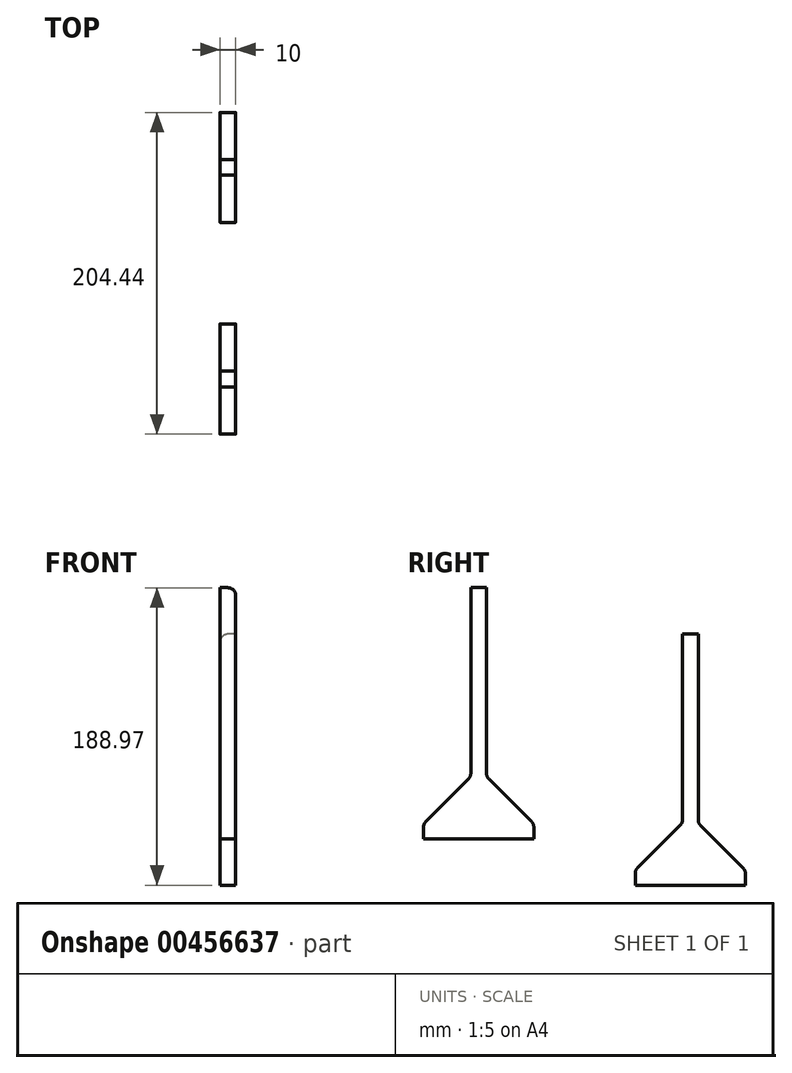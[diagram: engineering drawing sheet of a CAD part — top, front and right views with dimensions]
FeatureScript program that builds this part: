
annotation { "Feature Type Name" : "Feature", "Feature Type Description" : "" }
export const myFeature = defineFeature(function(context is Context, id is Id, definition is map)
    precondition{}
    {
        {
            var Q0;
            Q0=qCreatedBy(makeId("Right.planeOp"),FACE);
            var sketch = newSketch(context, id + "F0", { "sketchPlane" : qUnion([Q0])});
            skLineSegment(sketch, "E0", {"start": v(-4.56, 141.63) * mm, "end": v(-4.56, -8.37) * mm});
            skLineSegment(sketch, "E1", {"start": v(-4.56, 141.63) * mm, "end": v(5.44, 141.63) * mm});
            skLineSegment(sketch, "E2", {"start": v(5.44, 141.63) * mm, "end": v(5.44, -8.37) * mm});
            skLineSegment(sketch, "E3", {"start": v(-4.56, -8.37) * mm, "end": v(5.44, -8.37) * mm});
            skLineSegment(sketch, "E4", {"start": v(-4.56, -8.37) * mm, "end": v(-34.56, -8.37) * mm});
            skLineSegment(sketch, "E5", {"start": v(-34.56, -8.37) * mm, "end": v(-34.56, -17.85) * mm});
            skLineSegment(sketch, "E6", {"start": v(-34.56, -17.85) * mm, "end": v(35.44, -17.85) * mm});
            skLineSegment(sketch, "E7", {"start": v(5.44, -8.37) * mm, "end": v(35.44, -8.37) * mm});
            skLineSegment(sketch, "E8", {"start": v(35.44, -8.37) * mm, "end": v(35.44, -17.85) * mm});
            skLineSegment(sketch, "E9", {"start": v(-34.56, -8.37) * mm, "end": v(-4.56, 21.63) * mm});
            skLineSegment(sketch, "E10", {"start": v(-4.56, 21.63) * mm, "end": v(-4.56, -8.37) * mm});
            skLineSegment(sketch, "E11", {"start": v(5.44, -8.37) * mm, "end": v(5.44, 21.63) * mm});
            skLineSegment(sketch, "E12", {"start": v(5.44, 21.63) * mm, "end": v(35.44, -8.37) * mm});
            skLineSegment(sketch, "E13", {"start": v(129.88, 112.15) * mm, "end": v(129.88, -37.85) * mm});
            skLineSegment(sketch, "E14", {"start": v(129.88, 112.15) * mm, "end": v(139.88, 112.15) * mm});
            skLineSegment(sketch, "E15", {"start": v(139.88, 112.15) * mm, "end": v(139.88, -37.85) * mm});
            skLineSegment(sketch, "E16", {"start": v(129.88, -37.85) * mm, "end": v(139.88, -37.85) * mm});
            skLineSegment(sketch, "E17", {"start": v(129.88, -37.85) * mm, "end": v(99.88, -37.85) * mm});
            skLineSegment(sketch, "E18", {"start": v(99.88, -37.85) * mm, "end": v(99.88, -47.34) * mm});
            skLineSegment(sketch, "E19", {"start": v(99.88, -47.34) * mm, "end": v(169.88, -47.34) * mm});
            skLineSegment(sketch, "E20", {"start": v(139.88, -37.85) * mm, "end": v(169.88, -37.85) * mm});
            skLineSegment(sketch, "E21", {"start": v(169.88, -37.85) * mm, "end": v(169.88, -47.34) * mm});
            skLineSegment(sketch, "E22", {"start": v(99.88, -37.85) * mm, "end": v(129.88, -7.85) * mm});
            skLineSegment(sketch, "E23", {"start": v(129.88, -7.85) * mm, "end": v(129.88, -37.85) * mm});
            skLineSegment(sketch, "E24", {"start": v(139.88, -37.85) * mm, "end": v(139.88, -7.85) * mm});
            skLineSegment(sketch, "E25", {"start": v(139.88, -7.85) * mm, "end": v(169.88, -37.85) * mm});
            skSolve(sketch);
        }
        {
            var Q0;
            Q0=makeQuery(id+"F0.imprint","IMPRINT",FACE,{"disambiguationData":[TD([[makeQuery(id+"F0.imprint","IMPRINT",EDGE,{"derivedFrom":sQuery(id+"F0.wireOp",EDGE,"E0")}),1.0]])]});
            var Q1;
            Q1=makeQuery(id+"F0.imprint","IMPRINT",FACE,{"disambiguationData":[TD([[makeQuery(id+"F0.imprint","IMPRINT",EDGE,{"derivedFrom":sQuery(id+"F0.wireOp",EDGE,"E4")}),-1.0]])]});
            var Q2;
            Q2=makeQuery(id+"F0.imprint","IMPRINT",FACE,{"disambiguationData":[TD([[makeQuery(id+"F0.imprint","IMPRINT",EDGE,{"derivedFrom":sQuery(id+"F0.wireOp",EDGE,"E7")}),1.0]])]});
            var Q3;
            Q3=makeQuery(id+"F0.imprint","IMPRINT",FACE,{"disambiguationData":[TD([[makeQuery(id+"F0.imprint","IMPRINT",EDGE,{"derivedFrom":sQuery(id+"F0.wireOp",EDGE,"E3")}),-1.0]])]});
            extrude(context, id + "F1", {"entities" : qUnion([Q0, Q1, Q2, Q3]), "depth" : 10 * mm});
        }
        {
            var Q0;
            Q0=makeQuery(id+"F0.imprint","IMPRINT",FACE,{"disambiguationData":[TD([[makeQuery(id+"F0.imprint","IMPRINT",EDGE,{"derivedFrom":sQuery(id+"F0.wireOp",EDGE,"E13")}),1.0]])]});
            var Q1;
            Q1=makeQuery(id+"F0.imprint","IMPRINT",FACE,{"disambiguationData":[TD([[makeQuery(id+"F0.imprint","IMPRINT",EDGE,{"derivedFrom":sQuery(id+"F0.wireOp",EDGE,"E17")}),-1.0]])]});
            var Q2;
            Q2=makeQuery(id+"F0.imprint","IMPRINT",FACE,{"disambiguationData":[TD([[makeQuery(id+"F0.imprint","IMPRINT",EDGE,{"derivedFrom":sQuery(id+"F0.wireOp",EDGE,"E20")}),1.0]])]});
            var Q3;
            Q3=makeQuery(id+"F0.imprint","IMPRINT",FACE,{"disambiguationData":[TD([[makeQuery(id+"F0.imprint","IMPRINT",EDGE,{"derivedFrom":sQuery(id+"F0.wireOp",EDGE,"E16")}),-1.0]])]});
            extrude(context, id + "F2", {"entities" : qUnion([Q0, Q1, Q2, Q3]), "depth" : 10 * mm});
        }
        {
            var Q0;
            Q0=makeQuery(id+"F1.opExtrude","CAP_EDGE",EDGE,{"disambiguationData":[OSD([sQuery(id+"F0.wireOp",EDGE,"E1")])],"isStart":false});
            fillet(context, id + "F3", {"entities" : qUnion([Q0]), "radius" : 5.08 * mm, "tangentPropagation" : true, "allowEdgeOverflow" : false});
        }
        {
            var Q0;
            Q0=makeQuery(id+"F2.opExtrude","CAP_EDGE",EDGE,{"disambiguationData":[OSD([sQuery(id+"F0.wireOp",EDGE,"E14")])],"isStart":true});
            fillet(context, id + "F4", {"entities" : qUnion([Q0]), "radius" : 5.08 * mm, "tangentPropagation" : true, "allowEdgeOverflow" : false});
        }
        {
            var Q0;
            Q0=makeQuery(id+"F2.opExtrude","SWEPT_EDGE",EDGE,{"disambiguationData":[OSD([sQuery(id+"F0.wireOp",EDGE,"E20"),sQuery(id+"F0.wireOp",EDGE,"E21"),sQuery(id+"F0.wireOp",EDGE,"E25")])]});
            fillet(context, id + "F5", {"entities" : qUnion([Q0]), "radius" : 5.08 * mm, "tangentPropagation" : true, "allowEdgeOverflow" : false});
        }
        {
            var Q0;
            Q0=makeQuery(id+"F2.opExtrude","SWEPT_EDGE",EDGE,{"disambiguationData":[OSD([sQuery(id+"F0.wireOp",EDGE,"E17"),sQuery(id+"F0.wireOp",EDGE,"E18"),sQuery(id+"F0.wireOp",EDGE,"E22")])]});
            fillet(context, id + "F6", {"entities" : qUnion([Q0]), "radius" : 5.08 * mm, "tangentPropagation" : true, "allowEdgeOverflow" : false});
        }
        {
            var Q0;
            Q0=makeQuery(id+"F1.opExtrude","SWEPT_EDGE",EDGE,{"disambiguationData":[OSD([sQuery(id+"F0.wireOp",EDGE,"E4"),sQuery(id+"F0.wireOp",EDGE,"E5"),sQuery(id+"F0.wireOp",EDGE,"E9")])]});
            fillet(context, id + "F7", {"entities" : qUnion([Q0]), "radius" : 5.08 * mm, "tangentPropagation" : true, "allowEdgeOverflow" : false});
        }
        {
            var Q0;
            Q0=makeQuery(id+"F1.opExtrude","SWEPT_EDGE",EDGE,{"disambiguationData":[OSD([sQuery(id+"F0.wireOp",EDGE,"E7"),sQuery(id+"F0.wireOp",EDGE,"E8"),sQuery(id+"F0.wireOp",EDGE,"E12")])]});
            fillet(context, id + "F8", {"entities" : qUnion([Q0]), "radius" : 5.08 * mm, "tangentPropagation" : true, "allowEdgeOverflow" : false});
        }
        {
            var Q0;
            Q0=makeQuery(id+"F2.opExtrude","SWEPT_EDGE",EDGE,{"disambiguationData":[OSD([sQuery(id+"F0.wireOp",EDGE,"E15"),sQuery(id+"F0.wireOp",EDGE,"E24"),sQuery(id+"F0.wireOp",EDGE,"E25")])]});
            fillet(context, id + "F9", {"entities" : qUnion([Q0]), "radius" : 5.08 * mm, "tangentPropagation" : true, "allowEdgeOverflow" : false});
        }
        {
            var Q0;
            Q0=makeQuery(id+"F2.opExtrude","SWEPT_EDGE",EDGE,{"disambiguationData":[OSD([sQuery(id+"F0.wireOp",EDGE,"E13"),sQuery(id+"F0.wireOp",EDGE,"E22"),sQuery(id+"F0.wireOp",EDGE,"E23")])]});
            fillet(context, id + "F10", {"entities" : qUnion([Q0]), "radius" : 5.08 * mm, "tangentPropagation" : true, "allowEdgeOverflow" : false});
        }
        {
            var Q0;
            Q0=makeQuery(id+"F1.opExtrude","SWEPT_EDGE",EDGE,{"disambiguationData":[OSD([sQuery(id+"F0.wireOp",EDGE,"E0"),sQuery(id+"F0.wireOp",EDGE,"E9"),sQuery(id+"F0.wireOp",EDGE,"E10")])]});
            fillet(context, id + "F11", {"entities" : qUnion([Q0]), "radius" : 5.08 * mm, "tangentPropagation" : true, "allowEdgeOverflow" : false});
        }
        {
            var Q0;
            Q0=makeQuery(id+"F1.opExtrude","SWEPT_EDGE",EDGE,{"disambiguationData":[OSD([sQuery(id+"F0.wireOp",EDGE,"E2"),sQuery(id+"F0.wireOp",EDGE,"E11"),sQuery(id+"F0.wireOp",EDGE,"E12")])]});
            fillet(context, id + "F12", {"entities" : qUnion([Q0]), "radius" : 5.08 * mm, "tangentPropagation" : true, "allowEdgeOverflow" : false});
        }
    });
